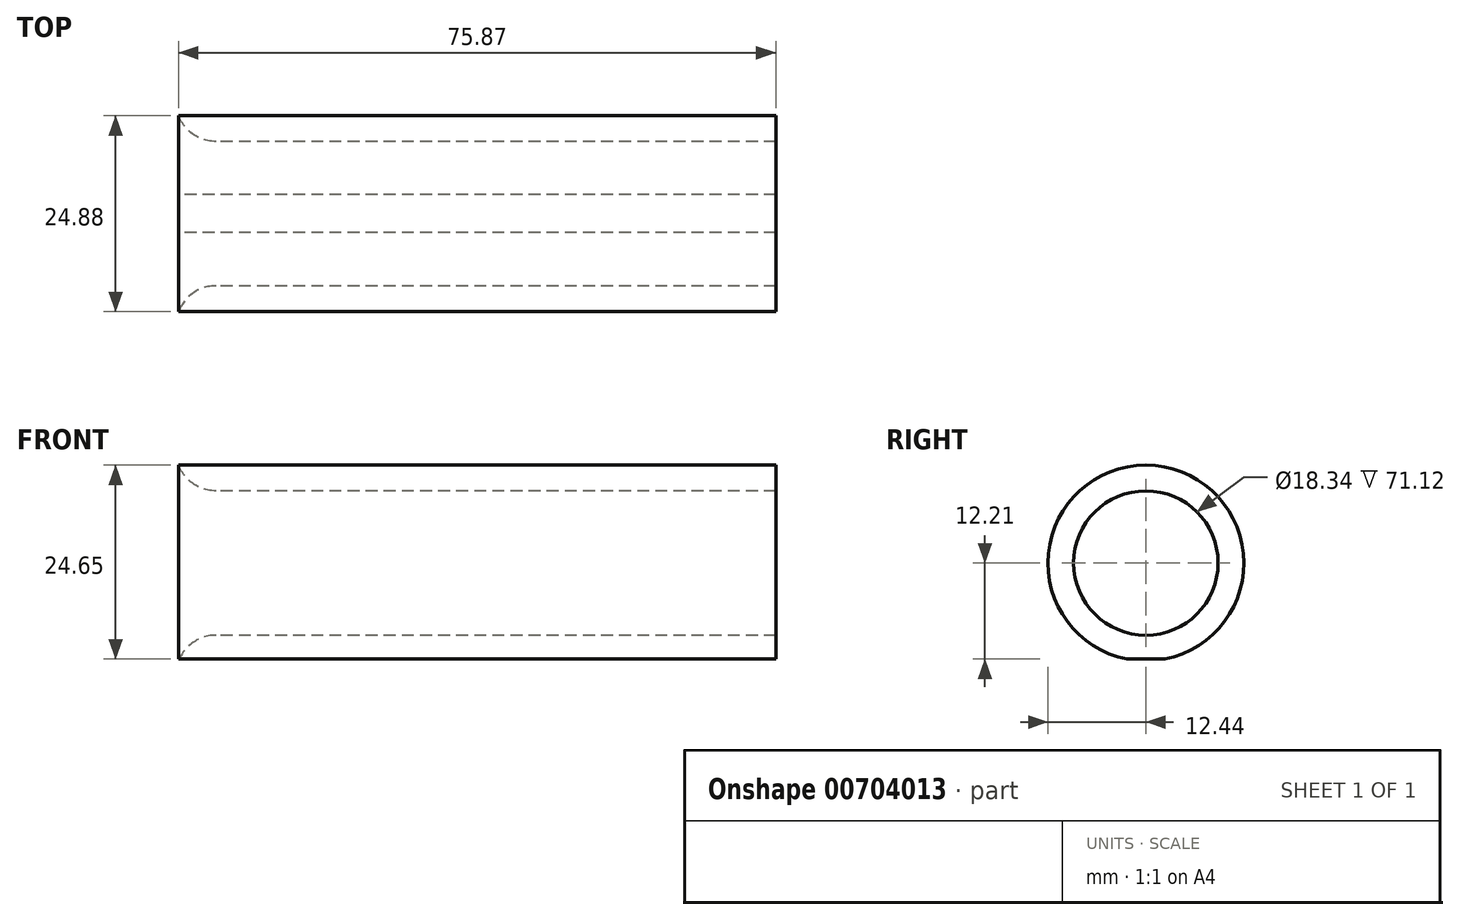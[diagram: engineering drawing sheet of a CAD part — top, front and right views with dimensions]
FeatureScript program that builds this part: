
annotation { "Feature Type Name" : "Feature", "Feature Type Description" : "" }
export const myFeature = defineFeature(function(context is Context, id is Id, definition is map)
    precondition{}
    {
        {
            var Q0;
            Q0=qCreatedBy(makeId("Right.planeOp"),FACE);
            var sketch = newSketch(context, id + "F0", { "sketchPlane" : qUnion([Q0])});
            skCircle(sketch, "E0", {"center": v(0, 0) * mm, "radius": 9.17 * mm});
            skCircle(sketch, "E1", {"center": v(0, 0) * mm, "radius": 12.44 * mm});
            skLineSegment(sketch, "E2", {"start": v(0, -12.2) * mm, "end": v(-2.41, -12.2) * mm});
            skLineSegment(sketch, "E3", {"start": v(-2.41, -12.2) * mm, "end": v(0, -12.2) * mm});
            skLineSegment(sketch, "E4", {"start": v(0, -12.2) * mm, "end": v(2.41, -12.2) * mm});
            skSolve(sketch);
        }
        {
            var Q0;
            Q0=makeQuery(id+"F0.imprint","IMPRINT",FACE,{"disambiguationData":[TD([[makeQuery(id+"F0.imprint","IMPRINT",EDGE,{"derivedFrom":sQuery(id+"F0.wireOp",EDGE,"E0")}),-1.0]])]});
            extrude(context, id + "F1", {"entities" : qUnion([Q0]), "depth" : 76.2 * mm, "offsetDistance" : 25.4 * mm});
        }
        {
            var Q0;
            Q0=makeQuery(id+"F1.opExtrude","CAP_EDGE",EDGE,{"disambiguationData":[OSD([sQuery(id+"F0.wireOp",EDGE,"E0")])],"isStart":true});
            fillet(context, id + "F2", {"entities" : qUnion([Q0]), "radius" : 5.08 * mm, "tangentPropagation" : true, "defaultsChanged" : false, "vertexSettings" : [], "allowEdgeOverflow" : false});
        }
    });
